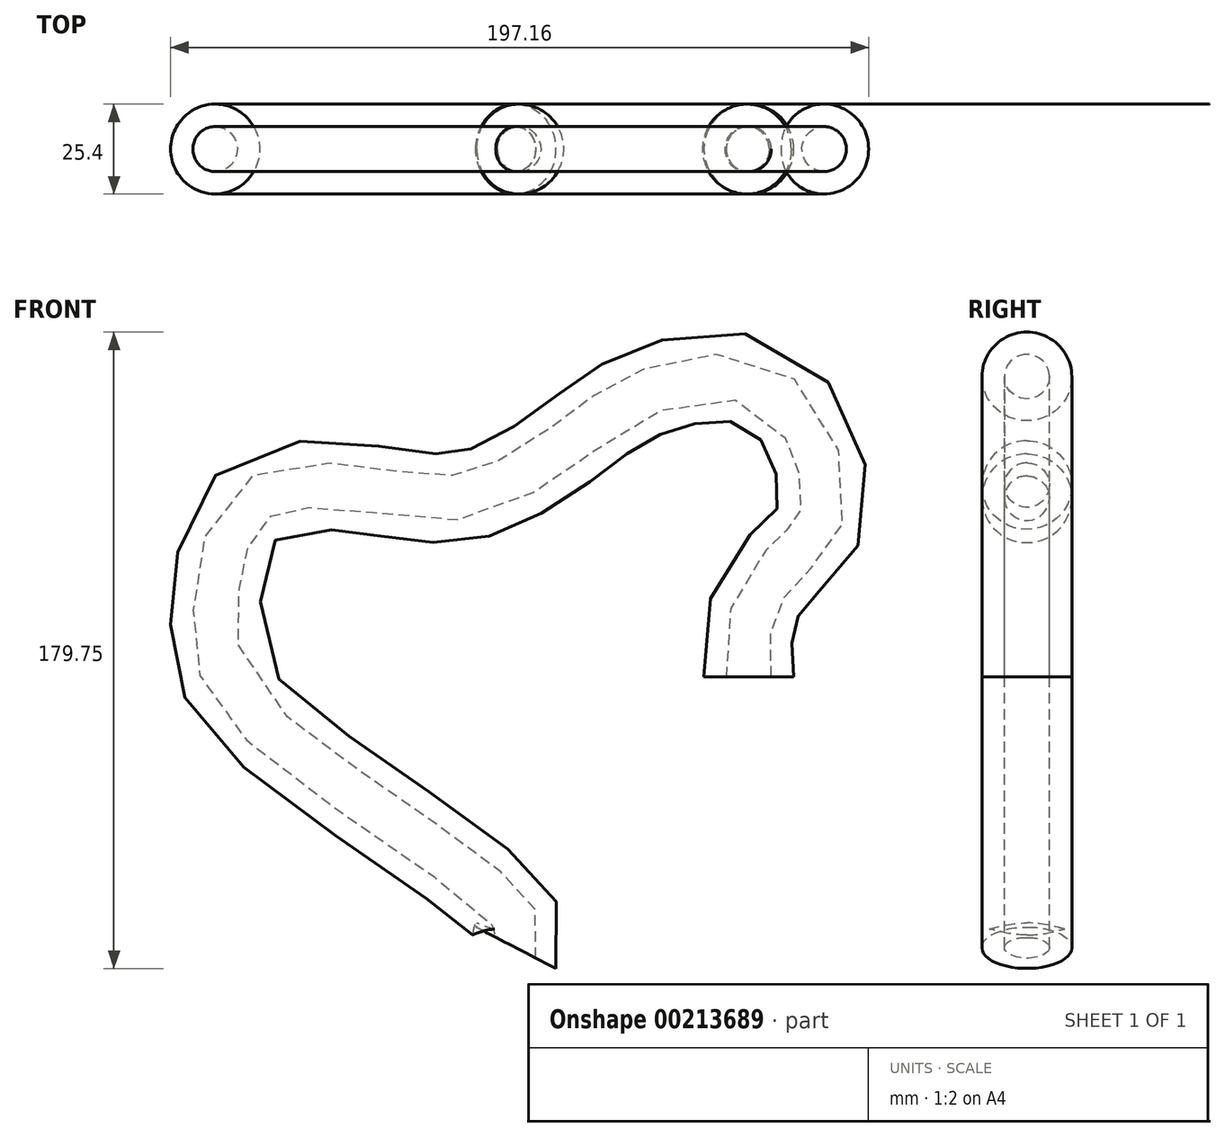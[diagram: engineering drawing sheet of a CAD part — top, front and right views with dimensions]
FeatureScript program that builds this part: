
annotation { "Feature Type Name" : "Feature", "Feature Type Description" : "" }
export const myFeature = defineFeature(function(context is Context, id is Id, definition is map)
    precondition{}
    {
        {
            var Q0;
            Q0=qCreatedBy(makeId("Top.planeOp"),FACE);
            var sketch = newSketch(context, id + "F0", { "sketchPlane" : qUnion([Q0])});
            skCircle(sketch, "E0", {"center": v(0, 0) * mm, "radius": 6.35 * mm});
            skCircle(sketch, "E1", {"center": v(0, 0) * mm, "radius": 12.7 * mm});
            skSolve(sketch);
        }
        {
            var Q0;
            Q0=qCreatedBy(makeId("Front.planeOp"),FACE);
            var sketch = newSketch(context, id + "F1", { "sketchPlane" : qUnion([Q0])});
            skFitSpline(sketch, "E2", {"points": [v(0, 0) * mm, v(2.03, 20.81) * mm, v(12.68, 34.64) * mm, v(21.09, 47.82) * mm, v(6.27, 81.1) * mm, v(-29.6, 80.13) * mm, v(-47.23, 68.92) * mm, v(-76.39, 51.94) * mm, v(-102.98, 52.26) * mm, v(-140.14, 49.38) * mm, v(-150.72, 16.05) * mm, v(-139.18, -11.82) * mm, v(-66.77, -67.25) * mm, v(-65.81, -76.54) * mm], "startDerivative": vector(-44.97, 283.8) * mm, "endDerivative": vector(-62.74, -188.52) * mm});
            skSolve(sketch);
        }
        {
            var Q0;
            Q0=makeQuery(id+"F0.imprint","IMPRINT",FACE,{"disambiguationData":[TD([[makeQuery(id+"F0.imprint","IMPRINT",EDGE,{"derivedFrom":sQuery(id+"F0.wireOp",EDGE,"E0")}),-1.0]])]});
            var Q1;
            Q1=sQuery(id+"F1.wireOp",EDGE,"E2");
            sweep(context, id + "F2", {"profiles" : qUnion([Q0]), "path" : qUnion([Q1])});
        }
    });
